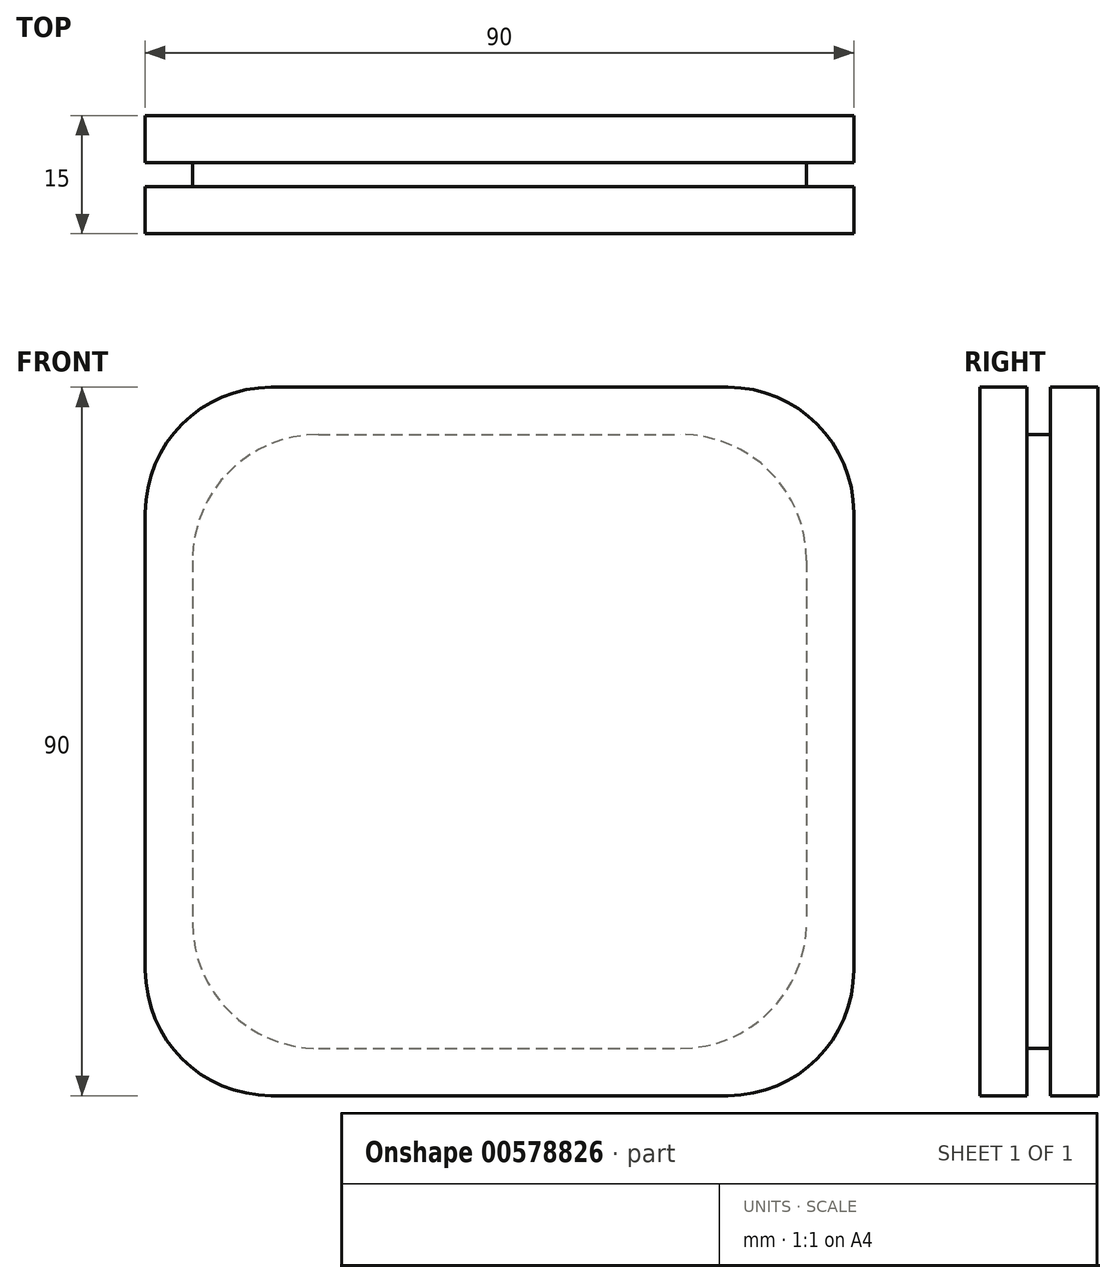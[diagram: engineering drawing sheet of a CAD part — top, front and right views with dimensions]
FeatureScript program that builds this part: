
annotation { "Feature Type Name" : "Feature", "Feature Type Description" : "" }
export const myFeature = defineFeature(function(context is Context, id is Id, definition is map)
    precondition{}
    {
        {
            var Q0;
            Q0=qCreatedBy(makeId("Front.planeOp"),FACE);
            var sketch = newSketch(context, id + "F0", { "sketchPlane" : qUnion([Q0])});
            skLineSegment(sketch, "E0.bottom", {"start": v(-29, 45) * mm, "end": v(29, 45) * mm});
            skLineSegment(sketch, "E0.top", {"start": v(-29, -45) * mm, "end": v(29, -45) * mm});
            skLineSegment(sketch, "E0.left", {"start": v(-45, 29) * mm, "end": v(-45, -29) * mm});
            skLineSegment(sketch, "E0.right", {"start": v(45, 29) * mm, "end": v(45, -29) * mm});
            skPoint(sketch, "E0.middle", {"position": v(0, 0) * mm});
            skPoint(sketch, "E1.visualSharp", {"position": v(-45, 45) * mm});
            skArc(sketch, "E1.filletArc", {"start": v(-29, 45) * mm, "mid": v(-40.31, 40.31) * mm, "end": v(-45, 29) * mm});
            skPoint(sketch, "E2.visualSharp", {"position": v(45, 45) * mm});
            skArc(sketch, "E2.filletArc", {"start": v(45, 29) * mm, "mid": v(40.31, 40.31) * mm, "end": v(29, 45) * mm});
            skPoint(sketch, "E3.visualSharp", {"position": v(-45, -45) * mm});
            skArc(sketch, "E3.filletArc", {"start": v(-45, -29) * mm, "mid": v(-40.31, -40.31) * mm, "end": v(-29, -45) * mm});
            skPoint(sketch, "E4.visualSharp", {"position": v(45, -45) * mm});
            skArc(sketch, "E4.filletArc", {"start": v(29, -45) * mm, "mid": v(40.31, -40.31) * mm, "end": v(45, -29) * mm});
            skSolve(sketch);
        }
        {
            var Q0;
            Q0 = qSketchRegion(id + "F0", true);
            extrude(context, id + "F1", {"entities" : qUnion([Q0]), "depth" : 6 * mm, "offsetDistance" : 25 * mm});
        }
        {
            var Q0;
            Q0=makeQuery(id+"F1.opExtrude","CAP_FACE",FACE,{"disambiguationData":[OSD([sQuery(id+"F0.wireOp",EDGE,"E0.bottom"),sQuery(id+"F0.wireOp",EDGE,"E0.top"),sQuery(id+"F0.wireOp",EDGE,"E0.left"),sQuery(id+"F0.wireOp",EDGE,"E0.right"),sQuery(id+"F0.wireOp",EDGE,"E1.filletArc"),sQuery(id+"F0.wireOp",EDGE,"E2.filletArc"),sQuery(id+"F0.wireOp",EDGE,"E3.filletArc"),sQuery(id+"F0.wireOp",EDGE,"E4.filletArc")])],"isStart":false});
            var sketch = newSketch(context, id + "F2", { "sketchPlane" : qUnion([Q0])});
            skLineSegment(sketch, "E5.bottom", {"start": v(-23, 39) * mm, "end": v(23, 39) * mm});
            skLineSegment(sketch, "E5.top", {"start": v(-23, -39) * mm, "end": v(23, -39) * mm});
            skLineSegment(sketch, "E5.left", {"start": v(-39, 23) * mm, "end": v(-39, -23) * mm});
            skLineSegment(sketch, "E5.right", {"start": v(39, 23) * mm, "end": v(39, -23) * mm});
            skPoint(sketch, "E5.middle", {"position": v(0, 0) * mm});
            skPoint(sketch, "E6.visualSharp", {"position": v(-39, 39) * mm});
            skArc(sketch, "E6.filletArc", {"start": v(-23, 39) * mm, "mid": v(-34.31, 34.31) * mm, "end": v(-39, 23) * mm});
            skPoint(sketch, "E7.visualSharp", {"position": v(39, 39) * mm});
            skArc(sketch, "E7.filletArc", {"start": v(39, 23) * mm, "mid": v(34.31, 34.31) * mm, "end": v(23, 39) * mm});
            skPoint(sketch, "E8.visualSharp", {"position": v(-39, -39) * mm});
            skArc(sketch, "E8.filletArc", {"start": v(-39, -23) * mm, "mid": v(-34.31, -34.31) * mm, "end": v(-23, -39) * mm});
            skPoint(sketch, "E9.visualSharp", {"position": v(39, -39) * mm});
            skArc(sketch, "E9.filletArc", {"start": v(23, -39) * mm, "mid": v(34.31, -34.31) * mm, "end": v(39, -23) * mm});
            skSolve(sketch);
        }
        {
            var Q0;
            Q0=makeQuery(id+"F2.imprint","IMPRINT",FACE,{"disambiguationData":[TD([[makeQuery(id+"F2.imprint","IMPRINT",EDGE,{"derivedFrom":sQuery(id+"F2.wireOp",EDGE,"E5.bottom")}),-1.0]])]});
            extrude(context, id + "F3", {"entities" : qUnion([Q0]), "depth" : 3 * mm, "offsetDistance" : 25 * mm});
        }
        {
            var Q0;
            Q0=makeQuery(id+"F3.opExtrude","CAP_FACE",FACE,{"disambiguationData":[OSD([sQuery(id+"F2.wireOp",EDGE,"E5.bottom"),sQuery(id+"F2.wireOp",EDGE,"E5.top"),sQuery(id+"F2.wireOp",EDGE,"E5.left"),sQuery(id+"F2.wireOp",EDGE,"E5.right"),sQuery(id+"F2.wireOp",EDGE,"E6.filletArc"),sQuery(id+"F2.wireOp",EDGE,"E7.filletArc"),sQuery(id+"F2.wireOp",EDGE,"E8.filletArc"),sQuery(id+"F2.wireOp",EDGE,"E9.filletArc")])],"isStart":false});
            var sketch = newSketch(context, id + "F4", { "sketchPlane" : qUnion([Q0])});
            skLineSegment(sketch, "E10.bottom", {"start": v(-29, 45) * mm, "end": v(29, 45) * mm});
            skLineSegment(sketch, "E10.top", {"start": v(-29, -45) * mm, "end": v(29, -45) * mm});
            skLineSegment(sketch, "E10.left", {"start": v(-45, 29) * mm, "end": v(-45, -29) * mm});
            skLineSegment(sketch, "E10.right", {"start": v(45, 29) * mm, "end": v(45, -29) * mm});
            skPoint(sketch, "E10.middle", {"position": v(0, 0) * mm});
            skPoint(sketch, "E11.visualSharp", {"position": v(-45, 45) * mm});
            skArc(sketch, "E11.filletArc", {"start": v(-29, 45) * mm, "mid": v(-40.31, 40.31) * mm, "end": v(-45, 29) * mm});
            skPoint(sketch, "E12.visualSharp", {"position": v(45, 45) * mm});
            skArc(sketch, "E12.filletArc", {"start": v(45, 29) * mm, "mid": v(40.31, 40.31) * mm, "end": v(29, 45) * mm});
            skPoint(sketch, "E13.visualSharp", {"position": v(-45, -45) * mm});
            skArc(sketch, "E13.filletArc", {"start": v(-45, -29) * mm, "mid": v(-40.31, -40.31) * mm, "end": v(-29, -45) * mm});
            skPoint(sketch, "E14.visualSharp", {"position": v(45, -45) * mm});
            skArc(sketch, "E14.filletArc", {"start": v(29, -45) * mm, "mid": v(40.31, -40.31) * mm, "end": v(45, -29) * mm});
            skSolve(sketch);
        }
        {
            var Q0;
            Q0 = qSketchRegion(id + "F4", true);
            extrude(context, id + "F5", {"entities" : qUnion([Q0]), "depth" : 6 * mm, "offsetDistance" : 25 * mm});
        }
    });
